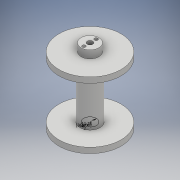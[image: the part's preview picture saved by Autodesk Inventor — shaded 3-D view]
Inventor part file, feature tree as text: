
AUTODESK INVENTOR PART (.ipt)
format: ipt  version: 2017 (Build 210142000, 142)  size: 194,048 bytes
history: native  units: mm
features: sketch x6, extrude x4, revolve x1
ambient origin geometry x8: Origin, YZ Plane, XZ Plane, XY Plane, X Axis, Y Axis, Z Axis, Center Point
bodies: Solid1 (feature_tree)
feature tree (11):
  revolve  "Revolution1"  Angle=90.0deg
  sketch  "Sketch3"  dims[d2=8.0mm d3=90.0deg]
  extrude  "Extrusion1"  TaperAngle=90.0deg  [1 undecoded]
  extrude  "Extrusion2"  TaperAngle=90.0deg  [1 undecoded]
  sketch  "Sketch5"  dims[d6=2.5mm d7=90.0deg]
  extrude  "Extrusion3"  TaperAngle=90.0deg  [1 undecoded]
  extrude  "Extrusion4"  TaperAngle=0.0deg  [1 undecoded]
  sketch  "Sketch1"  dims[d0=30.0mm d1=90.0deg]
  sketch  "Sketch4"  dims[d4=7.0mm d5=90.0deg]
  sketch  "Sketch6"  dims[d8=2.5mm d9=0.0mm]
  sketch  "Sketch7"  dims[d10=5.0mm d11=20.0mm d12=90.0deg d13=90.0deg d14=24.0mm d15=3.0mm d16=8.0mm d17=3.0mm d18=5.0mm d19=24.0mm d20=0.0mm d21=24.0mm d22=0.0mm d23=11.25mm d24=2.0mm d25=40.0mm d27=360.0deg d29=11.0mm d30=3.0mm d31=20.0mm d33=360.0deg d35=13.0mm d36=0.0mm d37=11.0mm d38=3.0mm d39=20.0mm d41=360.0deg d43=13.0mm d44=0.0mm d45=5.75mm d46=1.0mm]
note: 4 required parameter values undecoded (feature->parameter linkage not recoverable at this tier; creation-order binding heuristic only, values carry confidence <= 0.55)
